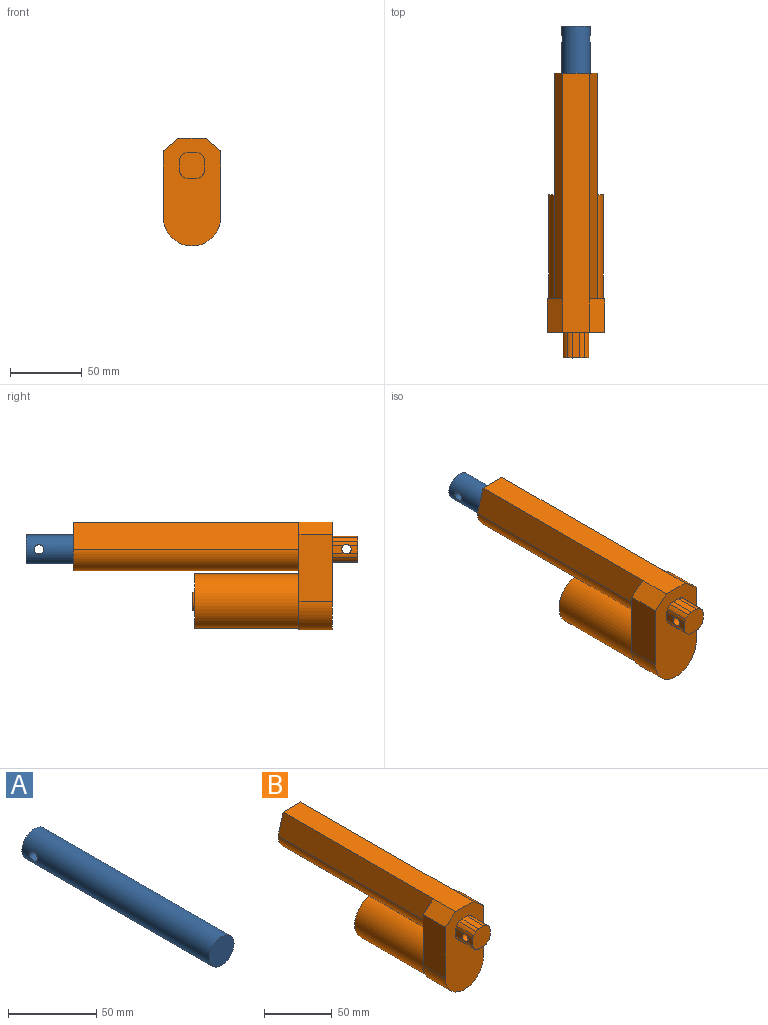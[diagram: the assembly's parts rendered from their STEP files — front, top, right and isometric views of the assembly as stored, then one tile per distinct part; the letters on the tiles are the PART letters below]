
ASSEMBLY  parts=2 mates=1
PART A: 4 faces, bbox 20x150x20 mm
  f0: cylinder r=10mm len=150mm, axis (0,1,0), area 9357.5mm2, adj f1,f2,f3
  f1: plane 20x20mm, normal (0,-1,0), area 314.2mm2, adj f0
  f2: plane 20x20mm, normal (0,1,0), area 314.2mm2, adj f0
  f3: cylinder r=3.25mm len=20mm, axis (-1,0,0), area 397.4mm2, adj f0
PART B: 45 faces, bbox 40x198x75 mm
  f0: plane 6.32x5.3mm, normal (1,0,0), area 27.4mm2, adj f1,f2,f31,f44
  f1: cylinder r=6.35mm len=17.75mm, axis (0,1,0), area 54mm2, adj f0,f18,f22,f27,f31,f44
  f2: cylinder r=6.35mm len=17.75mm, axis (0,1,0), area 55mm2, adj f0,f18,f22,f30,f31,f44
  f3: plane 6.32x5.3mm, normal (-1,0,0), area 27.4mm2, adj f4,f5,f31,f44
  f4: cylinder r=6.35mm len=17.75mm, axis (0,1,0), area 54mm2, adj f3,f18,f20,f28,f31,f44
  f5: cylinder r=6.35mm len=17.75mm, axis (0,1,0), area 55mm2, adj f3,f18,f20,f29,f31,f44
  f6: plane 75x40mm, normal (0,1,0), area 803.8mm2, adj f12,f13,f14,f15,f16,f32,f39,f40
  f7: plane 20x20mm, normal (0,1,0), area 314.2mm2, adj f27,f28,f29,f30,f36,f37,f38,f42
  f8: cylinder r=6.35mm len=180.25mm, axis (0,1,0), area 659.7mm2, adj f18,f30,f38,f42,f43
  f9: cylinder r=6.35mm len=180.25mm, axis (0,1,0), area 659.7mm2, adj f18,f29,f36,f42,f43
  f10: cylinder r=6.35mm len=180.25mm, axis (0,1,0), area 659.7mm2, adj f18,f28,f36,f37,f43
  f11: cylinder r=6.35mm len=180.25mm, axis (0,1,0), area 659.7mm2, adj f18,f27,f37,f38,f43
  f12: plane 23.25x10.75mm, normal (-0.64,0,0.77), area 325.5mm2, adj f6,f13,f17,f18
  f13: plane 46.03x23.25mm, normal (-1,0,0), area 1070.2mm2, adj f6,f12,f14,f18
  f14: cylinder r=20mm len=40mm, axis (0,1,0), area 1460.8mm2, adj f6,f13,f15,f18
  f15: plane 46.03x23.25mm, normal (1,0,0), area 1070.2mm2, adj f6,f14,f16,f18
  f16: plane 23.25x10.75mm, normal (0.64,0,0.77), area 325.5mm2, adj f6,f15,f17,f18
  f17: plane 180.25x18.5mm, normal (0,0,1), area 3334.6mm2, adj f12,f16,f18,f39,f41,f43
  f18: plane 75x40mm, normal (0,-1,0), area 2442.5mm2, adj f1,f2,f4,f5,f8,f9,f10,f11
  f19: plane 17.75x5.3mm, normal (0,0,-1), area 94.1mm2, adj f18,f25,f26,f31
  f20: plane 8.07x5.3mm, normal (-1,0,0), area 36.6mm2, adj f4,f5,f18,f44
  f21: plane 17.75x5.3mm, normal (0,0,1), area 94.1mm2, adj f18,f23,f24,f31
  f22: plane 8.07x5.3mm, normal (1,0,0), area 36.6mm2, adj f1,f2,f18,f44
  f23: cylinder r=6.35mm len=17.75mm, axis (0,1,0), area 56mm2, adj f18,f21,f27,f31
  f24: cylinder r=6.35mm len=17.75mm, axis (0,1,0), area 56mm2, adj f18,f21,f28,f31
  f25: cylinder r=6.35mm len=17.75mm, axis (0,1,0), area 56mm2, adj f18,f19,f29,f31
  f26: cylinder r=6.35mm len=17.75mm, axis (0,1,0), area 56mm2, adj f18,f19,f30,f31
  f27: cylinder r=10mm len=41mm, axis (0,1,0), area 148.8mm2, adj f1,f7,f11,f23,f31
  f28: cylinder r=10mm len=41mm, axis (0,1,0), area 148.8mm2, adj f4,f7,f10,f24,f31
  f29: cylinder r=10mm len=41mm, axis (0,1,0), area 148.8mm2, adj f5,f7,f9,f25,f31
  f30: cylinder r=10mm len=41mm, axis (0,1,0), area 148.8mm2, adj f2,f7,f8,f26,f31
  f31: plane 18x18mm, normal (0,-1,0), area 288.4mm2, adj f0,f1,f2,f3,f4,f5,f19,f21
  f32: cylinder r=19mm len=72.5mm, axis (0,-1,0), area 8655.1mm2, adj f6,f33
  f33: plane 38x38mm, normal (0,1,0), area 1006.4mm2, adj f32,f34
  f34: cylinder r=6.38mm len=12.75mm, axis (0,-1,0), area 60.1mm2, adj f33,f35
  f35: plane 12.75x12.75mm, normal (0,1,0), area 127.7mm2, adj f34
  f36: cylinder r=10mm len=157mm, axis (0,-1,0), area 1896.3mm2, adj f7,f9,f10,f43
  f37: cylinder r=10mm len=157mm, axis (0,-1,0), area 1896.3mm2, adj f7,f10,f11,f43
  f38: cylinder r=10mm len=157mm, axis (0,-1,0), area 1896.3mm2, adj f7,f8,f11,f43
  f39: plane 157x19mm, normal (-0.96,0,0.27), area 3101.1mm2, adj f6,f17,f40,f43
  f40: cylinder r=14.65mm len=157mm, axis (0,-1,0), area 7255.2mm2, adj f6,f39,f41,f43
  f41: plane 157x19mm, normal (0.96,0,0.27), area 3101.1mm2, adj f6,f17,f40,f43
  f42: cylinder r=10mm len=157mm, axis (0,-1,0), area 1896.3mm2, adj f7,f8,f9,f43
  f43: plane 33.74x29.3mm, normal (0,1,0), area 478.9mm2, adj f8,f9,f10,f11,f17,f36,f37,f38
  f44: cylinder r=3.25mm len=18mm, axis (1,0,0), area 367.4mm2, adj f0,f1,f2,f3,f4,f5,f20,f22
PLACE A rot(axis=(-0.05,0.15,0.99),0deg) t=(-51.23,204.89,-5.83)mm
PLACE B rot(axis=(-0.05,0.15,0.99),0deg) t=(-51.23,15.19,-18.81)mm
MATE slider A.f0 <-> B.f27  axis (0,1,0) through (-51.23,54.89,-5.83)mm
